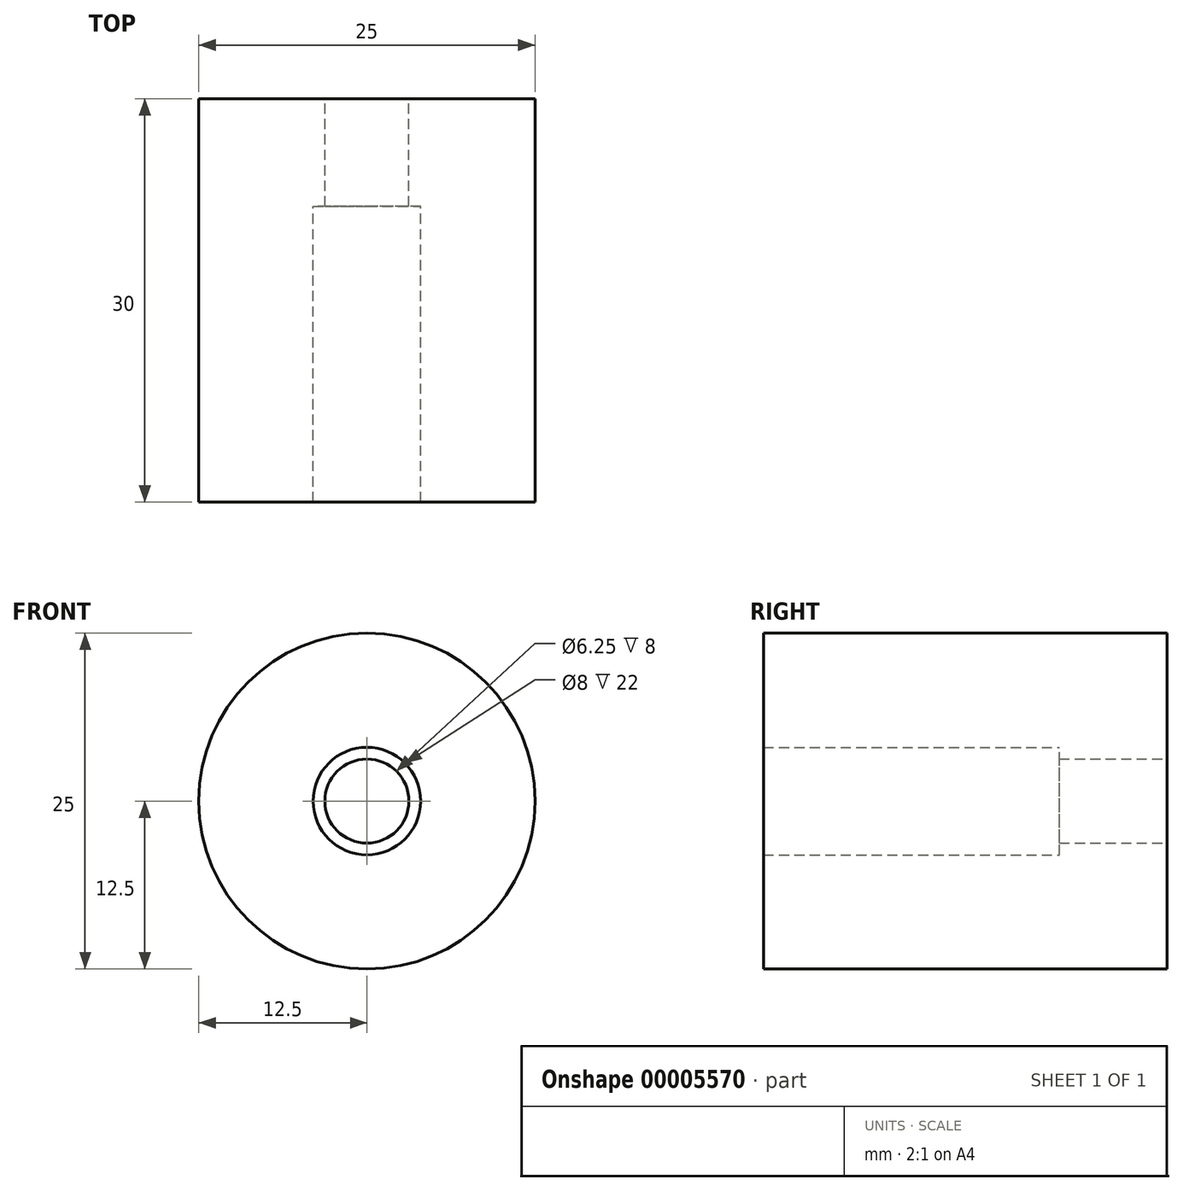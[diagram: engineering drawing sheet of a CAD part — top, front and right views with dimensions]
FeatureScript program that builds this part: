
annotation { "Feature Type Name" : "Feature", "Feature Type Description" : "" }
export const myFeature = defineFeature(function(context is Context, id is Id, definition is map)
    precondition{}
    {
        {
            var Q0;
            Q0=qCreatedBy(makeId("Front.planeOp"),FACE);
            var sketch = newSketch(context, id + "F0", { "sketchPlane" : qUnion([Q0])});
            skCircle(sketch, "E0", {"center": v(0, 0) * mm, "radius": 12.5 * mm});
            skCircle(sketch, "E1", {"center": v(0, 0) * mm, "radius": 3.12 * mm});
            skSolve(sketch);
        }
        {
            var Q0;
            Q0=makeQuery(id+"F0.imprint","IMPRINT",FACE,{"disambiguationData":[TD([[makeQuery(id+"F0.imprint","IMPRINT",EDGE,{"derivedFrom":sQuery(id+"F0.wireOp",EDGE,"E0")}),1.0]])]});
            extrude(context, id + "F1", {"entities" : qUnion([Q0]), "depth" : 30 * mm});
        }
        {
            var Q0;
            Q0=qCreatedBy(makeId("Front.planeOp"),FACE);
            cPlane(context, id + "F2", {"entities" : qUnion([Q0]), "cplaneType" : CPlaneType.OFFSET, "offset" : 8 * mm, "width" : 150 * mm, "height" : 150 * mm});
        }
        {
            var Q0;
            Q0=qCreatedBy(id+"F2.planeOp",FACE);
            var sketch = newSketch(context, id + "F3", { "sketchPlane" : qUnion([Q0])});
            skCircle(sketch, "E2", {"center": v(0, 0) * mm, "radius": 4 * mm});
            skCircle(sketch, "E3", {"center": v(0, 0) * mm, "radius": 12.5 * mm, "construction": true});
            skSolve(sketch);
        }
        {
            var Q0;
            Q0=makeQuery(id+"F3.imprint","IMPRINT",FACE,{"disambiguationData":[TD([[makeQuery(id+"F3.imprint","IMPRINT",EDGE,{"derivedFrom":sQuery(id+"F3.wireOp",EDGE,"E2")}),1.0]])]});
            var Q1;
            Q1=makeQuery(id+"F1.opExtrude","CAP_FACE",FACE,{"disambiguationData":[OSD([sQuery(id+"F0.wireOp",EDGE,"E0"),sQuery(id+"F0.wireOp",EDGE,"E1")])],"isStart":false});
            extrude(context, id + "F4", {"entities" : qUnion([Q0]), "operationType" : NewBodyOperationType.REMOVE, "endBound" : BoundingType.UP_TO_SURFACE, "endBoundEntityFace" : qUnion([Q1]), "depth" : 25 * mm});
        }
    });
